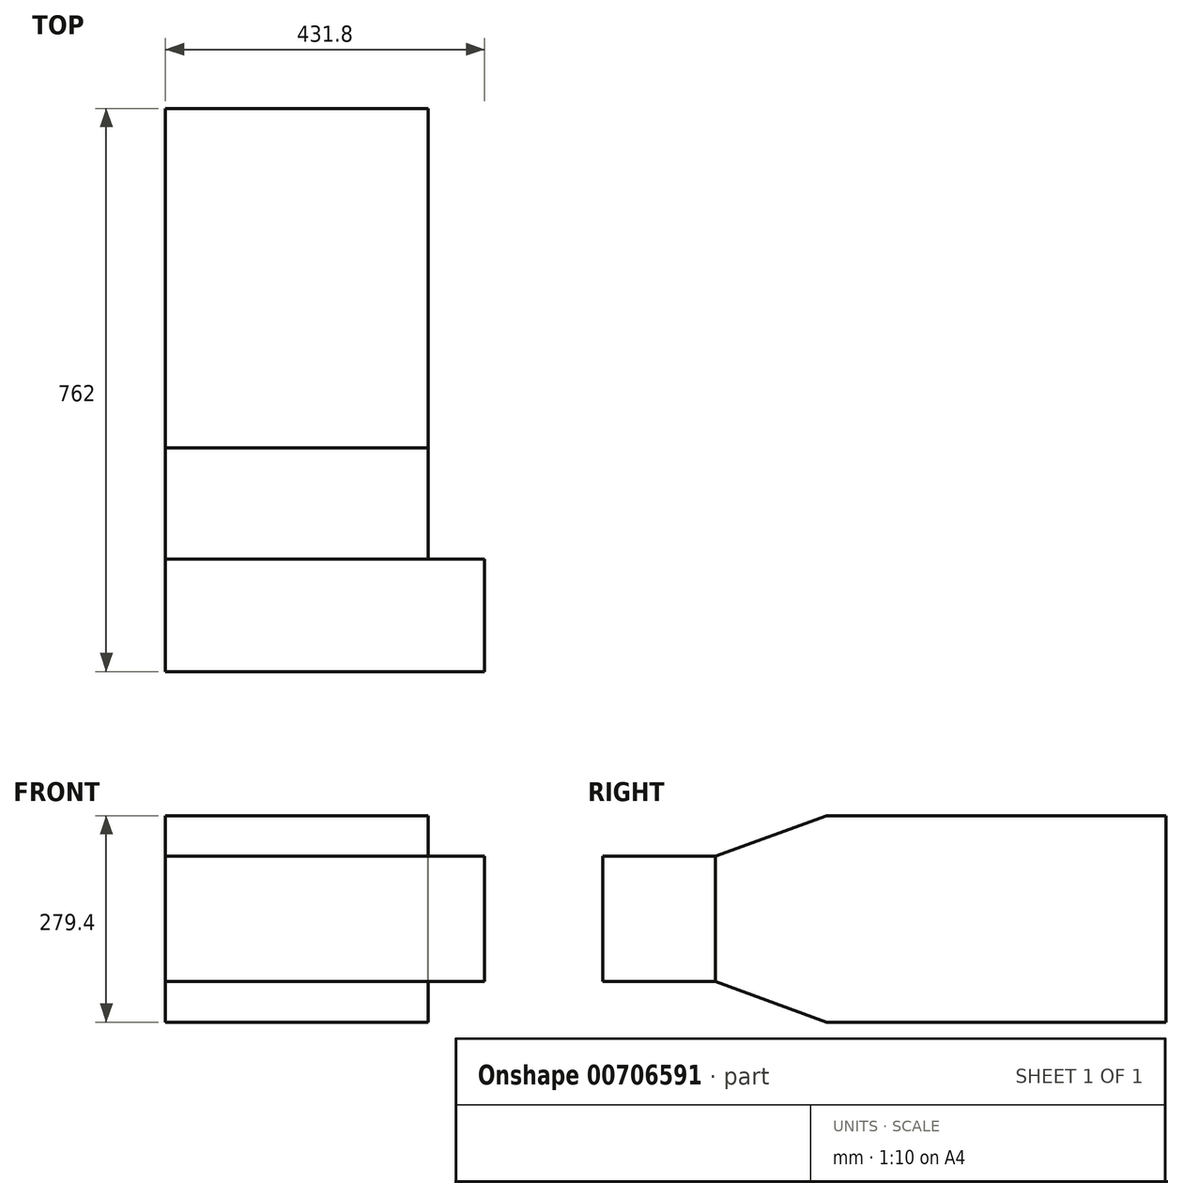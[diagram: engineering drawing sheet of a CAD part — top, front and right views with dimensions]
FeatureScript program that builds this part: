
annotation { "Feature Type Name" : "Feature", "Feature Type Description" : "" }
export const myFeature = defineFeature(function(context is Context, id is Id, definition is map)
    precondition{}
    {
        {
            var Q0;
            Q0=qCreatedBy(makeId("Front.planeOp"),FACE);
            var sketch = newSketch(context, id + "F0", { "sketchPlane" : qUnion([Q0])});
            skLineSegment(sketch, "E0.bottom", {"start": v(-215.9, -139.7) * mm, "end": v(215.9, -139.7) * mm});
            skLineSegment(sketch, "E0.top", {"start": v(-215.9, 139.7) * mm, "end": v(215.9, 139.7) * mm});
            skLineSegment(sketch, "E0.left", {"start": v(-215.9, -139.7) * mm, "end": v(-215.9, 139.7) * mm});
            skLineSegment(sketch, "E0.right", {"start": v(215.9, -139.7) * mm, "end": v(215.9, 139.7) * mm});
            skPoint(sketch, "E0.middle", {"position": v(0, 0) * mm});
            skSolve(sketch);
        }
        {
            var Q0;
            Q0=makeQuery(id+"F0.imprint","IMPRINT",FACE,{"disambiguationData":[TD([[makeQuery(id+"F0.imprint","IMPRINT",EDGE,{"derivedFrom":sQuery(id+"F0.wireOp",EDGE,"E0.bottom")}),1.0]])]});
            extrude(context, id + "F1", {"entities" : qUnion([Q0]), "depth" : 762 * mm, "offsetDistance" : 25.4 * mm});
        }
        {
            var Q0;
            Q0=makeQuery(id+"F1.opExtrude","CAP_FACE",FACE,{"disambiguationData":[OSD([sQuery(id+"F0.wireOp",EDGE,"E0.bottom"),sQuery(id+"F0.wireOp",EDGE,"E0.top"),sQuery(id+"F0.wireOp",EDGE,"E0.left"),sQuery(id+"F0.wireOp",EDGE,"E0.right")])],"isStart":true});
            var sketch = newSketch(context, id + "F2", { "sketchPlane" : qUnion([Q0])});
            skLineSegment(sketch, "E1", {"start": v(-215.9, 139.7) * mm, "end": v(-215.9, -139.7) * mm});
            skLineSegment(sketch, "E2", {"start": v(-215.9, -139.7) * mm, "end": v(-139.7, -139.7) * mm});
            skLineSegment(sketch, "E3", {"start": v(-139.7, -139.7) * mm, "end": v(-139.7, 139.7) * mm});
            skLineSegment(sketch, "E4", {"start": v(-139.7, 139.7) * mm, "end": v(-215.9, 139.7) * mm});
            skSolve(sketch);
        }
        {
            var Q0;
            Q0 = qSketchRegion(id + "F2", true);
            extrude(context, id + "F3", {"entities" : qUnion([Q0]), "operationType" : NewBodyOperationType.REMOVE, "oppositeDirection" : true, "depth" : 609.6 * mm, "offsetDistance" : 25.4 * mm});
        }
        {
            var Q0;
            Q0=makeQuery(id+"F1.opExtrude","SWEPT_FACE",FACE,{"disambiguationData":[OSD([sQuery(id+"F0.wireOp",EDGE,"E0.right")])]});
            var sketch = newSketch(context, id + "F4", { "sketchPlane" : qUnion([Q0])});
            skLineSegment(sketch, "E5", {"start": v(-762, 84.82) * mm, "end": v(-609.6, 84.82) * mm});
            skLineSegment(sketch, "E6", {"start": v(-457.2, 140.54) * mm, "end": v(-609.6, 84.82) * mm});
            skLineSegment(sketch, "E7", {"start": v(-457.2, 140.54) * mm, "end": v(-762, 139.7) * mm});
            skLineSegment(sketch, "E8", {"start": v(-762, 139.7) * mm, "end": v(-762, 84.82) * mm});
            skLineSegment(sketch, "E9.MirrorCS", {"start": v(-762, -139.7) * mm, "end": v(-762, -84.82) * mm});
            skLineSegment(sketch, "E10.MirrorCS", {"start": v(-762, -84.82) * mm, "end": v(-609.6, -84.82) * mm});
            skLineSegment(sketch, "E11.MirrorCS", {"start": v(-457.2, -140.54) * mm, "end": v(-762, -139.7) * mm});
            skLineSegment(sketch, "E12.MirrorCS", {"start": v(-457.2, -140.54) * mm, "end": v(-609.6, -84.82) * mm});
            skSolve(sketch);
        }
        {
            var Q0;
            Q0 = qSketchRegion(id + "F4", true);
            extrude(context, id + "F5", {"entities" : qUnion([Q0]), "operationType" : NewBodyOperationType.REMOVE, "endBound" : BoundingType.THROUGH_ALL, "oppositeDirection" : true, "depth" : 25.4 * mm, "offsetDistance" : 25.4 * mm});
        }
    });
